# Revit family: Sanitary_Taps&Mixers_Zurn_Z821B0-XL
name_source: partatom
category: Plumbing Fixtures
units: mm (PartAtom-declared; Revit-internal decimal feet)

## family parameters
Cut with Voids When Loaded = No
Host = Face
Maintain Annotation Orientation = No
OmniClass Number = 23.45.55.14
OmniClass Title = Single Faucets
Part Type = Normal
Room Calculation Point = No
Round Connector Dimension = Use Radius
Shared = No

## types (1)
- Z821B0-XL (Gooseneck Faucet)
    ADA Compliance = Yes
    Assembly Code = D2010.60
    CW Connection = Yes
    CWFU = 1
    Default Elevation = 34"
    Description = AquaSpec® deck-mount 5-3/8 in  gooseneckspout
    Flow  Rate = 2 GPM
    HW Connection = No
    HWFU = 0
    Height from Spout Base to Areator = 7 1/2"
    Inlet Connection Size (inch) = 1/2"
    Lead- Free Compliant = Yes
    Main Material = Brass - Zurn - Polished Chrome-Finish
    Manufacturer = Zurn Water, LLC
    Manufacturer Brand = Zurn
    Model = Z826B0-XL
    Modified Date = 01/13/2026
    Product Documentation Link = https://files.zurn.com
    Product Installation Sheet URL = https://files.zurn.com
    Product Page URL = https://www.zurn.com
    Spout Height from Base = 11"
    Spout length = 5 1/2"
    Types of Outlet = Laminar
    URL = http://www.zurn.com
    Vent Connection = No
    WFU = 0
    Waste Connection = No
    Water Sense Compliance = No

## geometry (parser evidence)
native form markers: Blend x4, Sweep x4
no freeform markers — native parametric forms only
